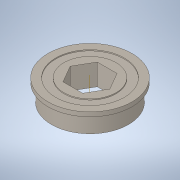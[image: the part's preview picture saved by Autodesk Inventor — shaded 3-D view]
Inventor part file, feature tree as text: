
AUTODESK INVENTOR PART (.ipt)
format: ipt  version: 2020 (Build 240168000, 168)  size: 160,768 bytes
history: native  units: in
note: dims shown in document units (in); Inventor stores cm internally (conversion verified against a paired STEP export)
features: revolve x1, sketch x1, other x1
ambient origin geometry x8: Origin, YZ Plane, XZ Plane, XY Plane, X Axis, Y Axis, Z Axis, Center Point
bodies: Solid1 (feature_tree)
feature tree (3):
  revolve  "Revolution1"  [1 undecoded]
  sketch  "Sketch1"  dims[d0=90.0deg]
  other  "Cut-Extrude1"
note: 1 required parameter value undecoded (feature->parameter linkage not recoverable at this tier; creation-order binding heuristic only, values carry confidence <= 0.55)
